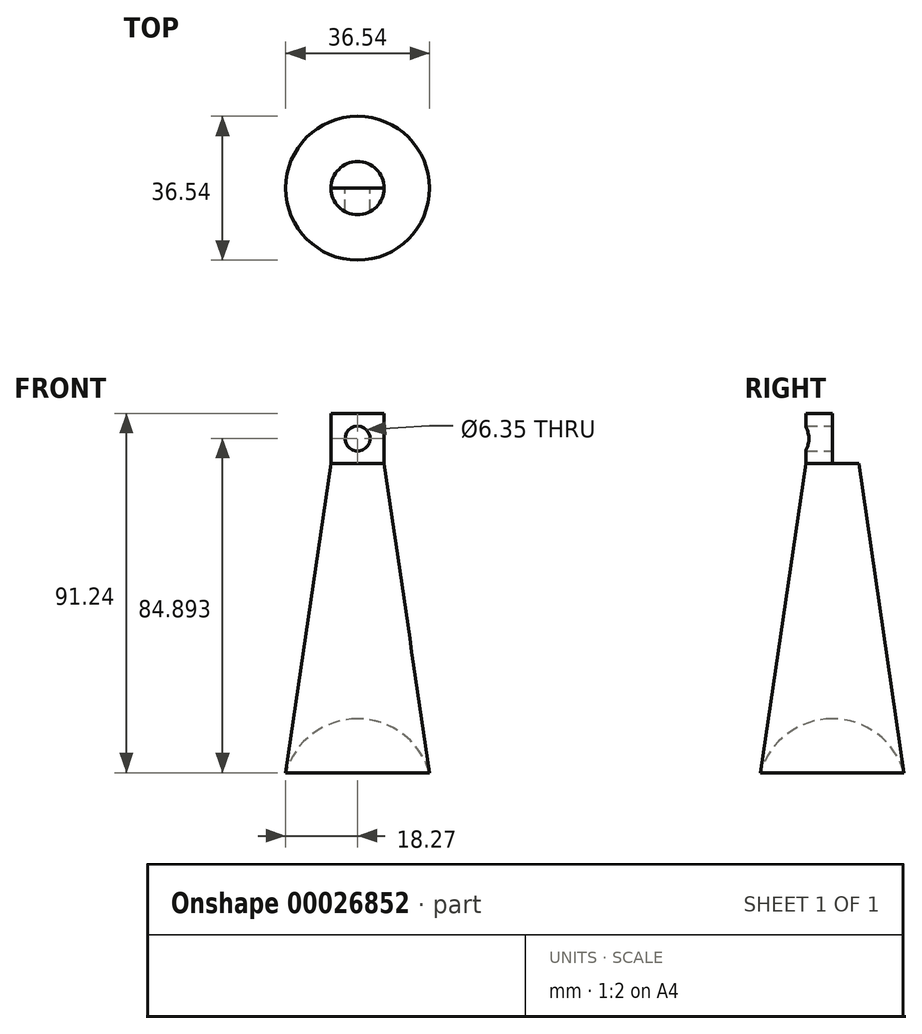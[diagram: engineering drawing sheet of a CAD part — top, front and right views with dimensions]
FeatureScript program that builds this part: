
annotation { "Feature Type Name" : "Feature", "Feature Type Description" : "" }
export const myFeature = defineFeature(function(context is Context, id is Id, definition is map)
    precondition{}
    {
        {
            var Q0;
            Q0=qCreatedBy(makeId("Front.planeOp"),FACE);
            var sketch = newSketch(context, id + "F0", { "sketchPlane" : qUnion([Q0])});
            skArc(sketch, "E0", {"start": v(19.05, -27.72) * mm, "mid": v(13.44, -14.3) * mm, "end": v(0, -8.76) * mm});
            skLineSegment(sketch, "E1", {"start": v(19.05, -27.72) * mm, "end": v(6.74, 56.11) * mm});
            skLineSegment(sketch, "E2", {"start": v(6.74, 56.11) * mm, "end": v(0, 56.11) * mm});
            skLineSegment(sketch, "E3", {"start": v(0, 56.11) * mm, "end": v(0, -8.76) * mm});
            skSolve(sketch);
        }
        {
            var Q0;
            {var subQ1=sQuery(id+"F0.wireOp",EDGE,"E2");Q0=makeQuery(id+"F0.imprint","IMPRINT",FACE,{"disambiguationData":[TD([[makeQuery(id+"F0.imprint","IMPRINT",EDGE,{"derivedFrom":subQ1}),1.0]])]});}
            var Q1;
            Q1=sQuery(id+"F0.wireOp",EDGE,"E3");
            revolve(context, id + "F1", {"entities" : qUnion([Q0]), "axis" : qUnion([Q1]), "revolveType" : RevolveType.FULL});
        }
        {
            var Q0;
            Q0=makeQuery(id+"F1.opRevolve","SWEPT_FACE",FACE,{"disambiguationData":[OSD([sQuery(id+"F0.wireOp",EDGE,"E2")])]});
            var sketch = newSketch(context, id + "F2", { "sketchPlane" : qUnion([Q0])});
            skLineSegment(sketch, "E4", {"start": v(-6.74, 0) * mm, "end": v(6.74, 0) * mm});
            skSolve(sketch);
        }
        {
            var Q0;
            {var subQ1=sQuery(id+"F2.wireOp",EDGE,"E4");Q0=makeQuery(id+"F2.imprint","IMPRINT",FACE,{"disambiguationData":[TD([[makeQuery(id+"F2.imprint","IMPRINT",EDGE,{"derivedFrom":subQ1}),-1.0]])]});}
            extrude(context, id + "F3", {"entities" : qUnion([Q0]), "operationType" : NewBodyOperationType.ADD, "depth" : 12.7 * mm});
        }
        {
            var Q0;
            Q0=makeQuery(id+"F3.opExtrude","SWEPT_FACE",FACE,{"disambiguationData":[OSD([sQuery(id+"F2.wireOp",EDGE,"E4")])]});
            var sketch = newSketch(context, id + "F4", { "sketchPlane" : qUnion([Q0])});
            skCircle(sketch, "E5", {"center": v(0, 62.46) * mm, "radius": 3.18 * mm});
            skPoint(sketch, "E6.orphan", {"position": v(-6.74, 62.46) * mm});
            skPoint(sketch, "E7.end.orphan", {"position": v(6.74, 62.46) * mm});
            skPoint(sketch, "E8.orphan", {"position": v(0, 68.81) * mm});
            skPoint(sketch, "E9.end.orphan", {"position": v(0, 56.11) * mm});
            skSolve(sketch);
        }
        {
            var Q0;
            Q0=sQuery(id+"F4.wireOp",VERTEX,"E5.center");
            var Q1;
            Q1=makeQuery(id+"F1.opRevolve","SWEPT_BODY",BODY,{"disambiguationData":[OSD([sQuery(id+"F0.wireOp",EDGE,"E0"),sQuery(id+"F0.wireOp",EDGE,"E1"),sQuery(id+"F0.wireOp",EDGE,"E2"),sQuery(id+"F0.wireOp",EDGE,"E3")])]});
            hole(context, id + "F5", {"style" : HoleStyle.SIMPLE, "holeDiameter" : 6.35 * mm, "endStyle" : HoleEndStyle.THROUGH, "locations" : qUnion([Q0]), "scope" : qUnion([Q1])});
        }
    });
